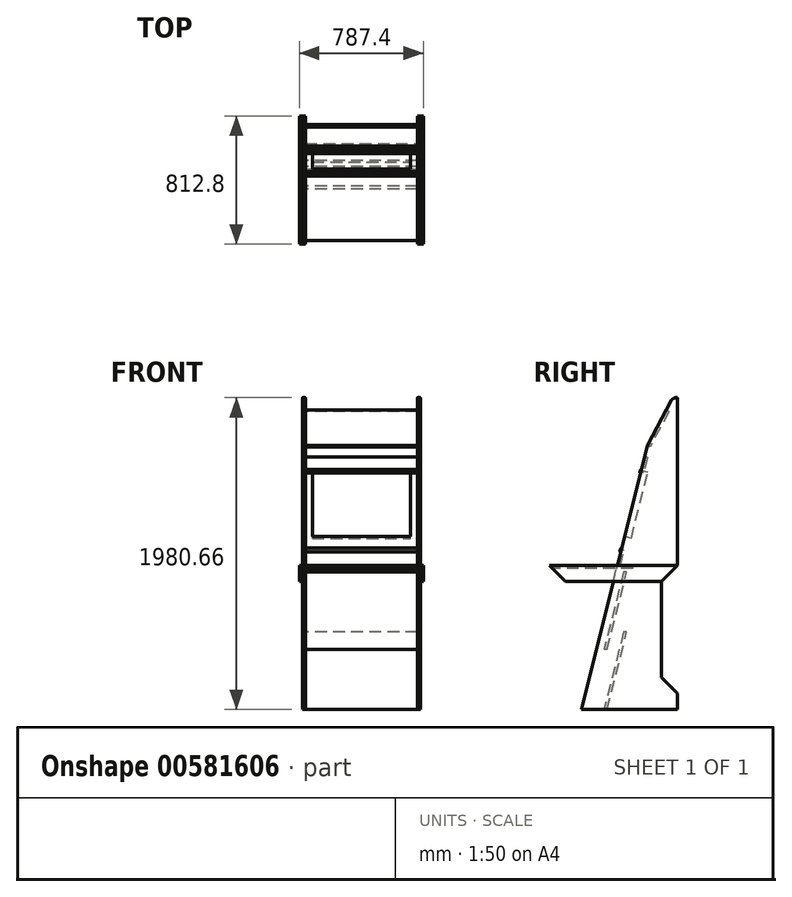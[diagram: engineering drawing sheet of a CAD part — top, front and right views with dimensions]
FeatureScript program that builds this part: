
annotation { "Feature Type Name" : "Feature", "Feature Type Description" : "" }
export const myFeature = defineFeature(function(context is Context, id is Id, definition is map)
    precondition{}
    {
        {
            var Q0;
            Q0=qCreatedBy(makeId("Right.planeOp"),FACE);
            var sketch = newSketch(context, id + "F0", { "sketchPlane" : qUnion([Q0])});
            skLineSegment(sketch, "E0.bottom", {"start": v(0, -978.45) * mm, "end": v(-609.6, -978.45) * mm});
            skLineSegment(sketch, "E0.left", {"start": v(0, -978.45) * mm, "end": v(0, 1053.55) * mm});
            skLineSegment(sketch, "E1", {"start": v(-609.6, -978.45) * mm, "end": v(-190.5, 697.95) * mm});
            skLineSegment(sketch, "E2", {"start": v(0, 1053.55) * mm, "end": v(-190.5, 697.95) * mm});
            skSolve(sketch);
        }
        {
            var Q0;
            Q0 = qSketchRegion(id + "F0", true);
            extrude(context, id + "F1", {"entities" : qUnion([Q0]), "depth" : 19.05 * mm, "offsetDistance" : 25.4 * mm});
        }
        {
            var Q0;
            Q0=makeQuery(id+"F1.opExtrude","CAP_FACE",FACE,{"disambiguationData":[OSD([sQuery(id+"F0.wireOp",EDGE,"E0.bottom"),sQuery(id+"F0.wireOp",EDGE,"E0.left"),sQuery(id+"F0.wireOp",EDGE,"E1"),sQuery(id+"F0.wireOp",EDGE,"E2")])],"isStart":false});
            var sketch = newSketch(context, id + "F2", { "sketchPlane" : qUnion([Q0])});
            skLineSegment(sketch, "E3.bottom", {"start": v(0, -876.85) * mm, "end": v(-101.6, -775.25) * mm});
            skLineSegment(sketch, "E3.left", {"start": v(0, -876.85) * mm, "end": v(0, -64.05) * mm});
            skLineSegment(sketch, "E3.right", {"start": v(-101.6, -775.25) * mm, "end": v(-101.6, -165.65) * mm});
            skLineSegment(sketch, "E4", {"start": v(0, -64.05) * mm, "end": v(-101.6, -165.65) * mm});
            skSolve(sketch);
        }
        {
            var Q0;
            Q0 = qSketchRegion(id + "F2", true);
            extrude(context, id + "F3", {"entities" : qUnion([Q0]), "operationType" : NewBodyOperationType.REMOVE, "oppositeDirection" : true, "depth" : 25.4 * mm, "offsetDistance" : 25.4 * mm});
        }
        {
            var Q0;
            Q0=makeQuery(id+"F1.opExtrude","SWEPT_BODY",BODY,{"disambiguationData":[OSD([sQuery(id+"F0.wireOp",EDGE,"E0.bottom"),sQuery(id+"F0.wireOp",EDGE,"E0.left"),sQuery(id+"F0.wireOp",EDGE,"E1"),sQuery(id+"F0.wireOp",EDGE,"E2")])]});
            transform(context, id + "F4", {"entities" : qUnion([Q0]), "transformType" : TransformType.TRANSLATION_3D, "dx" : 730.25 * mm, "dy" : 0 * mm, "dz" : 0 * mm, "makeCopy" : true});
        }
        {
            var Q0;
            Q0=makeQuery(id+"F4.opPattern","COPY",FACE,{"derivedFrom":makeQuery(id+"F1.opExtrude","CAP_FACE",FACE,{"disambiguationData":[OSD([sQuery(id+"F0.wireOp",EDGE,"E0.bottom"),sQuery(id+"F0.wireOp",EDGE,"E0.left"),sQuery(id+"F0.wireOp",EDGE,"E1"),sQuery(id+"F0.wireOp",EDGE,"E2")])],"isStart":false}),"instanceName":"1"});
            var sketch = newSketch(context, id + "F5", { "sketchPlane" : qUnion([Q0])});
            skLineSegment(sketch, "E5.bottom", {"start": v(0, -64.05) * mm, "end": v(-812.8, -64.05) * mm});
            skLineSegment(sketch, "E5.left", {"start": v(0, -64.05) * mm, "end": v(-101.6, -165.65) * mm});
            skLineSegment(sketch, "E6", {"start": v(-101.6, -165.65) * mm, "end": v(-711.2, -165.65) * mm});
            skLineSegment(sketch, "E7", {"start": v(-711.2, -165.65) * mm, "end": v(-812.8, -64.05) * mm});
            skSolve(sketch);
        }
        {
            var Q0;
            {var subQ0=sQuery(id+"F5.wireOp",EDGE,"E5.left");Q0=makeQuery(id+"F5.imprint","IMPRINT",FACE,{"disambiguationData":[TD([[makeQuery(id+"F5.imprint","IMPRINT",EDGE,{"derivedFrom":subQ0}),-1.0]])]});}
            var Q1;
            {var subQ0=sQuery(id+"F5.wireOp",EDGE,"E7");Q1=makeQuery(id+"F5.imprint","IMPRINT",FACE,{"disambiguationData":[TD([[makeQuery(id+"F5.imprint","IMPRINT",EDGE,{"derivedFrom":subQ0}),-1.0]])]});}
            extrude(context, id + "F6", {"entities" : qUnion([Q0, Q1]), "depth" : 19.05 * mm, "offsetDistance" : 25.4 * mm});
        }
        {
            var Q0;
            Q0=makeQuery(id+"F6.opExtrude","SWEPT_BODY",BODY,{"disambiguationData":[OSD([sQuery(id+"F5.wireOp",EDGE,"E5.bottom"),sQuery(id+"F5.wireOp",EDGE,"E5.left"),sQuery(id+"F5.wireOp",EDGE,"E6"),sQuery(id+"F5.wireOp",EDGE,"E7")])]});
            transform(context, id + "F7", {"entities" : qUnion([Q0]), "transformType" : TransformType.TRANSLATION_3D, "dx" : -768.35 * mm, "dy" : 0 * mm, "dz" : 0 * mm, "makeCopy" : true});
        }
        {
            var Q0;
            Q0=makeQuery(id+"F1.opExtrude","CAP_FACE",FACE,{"disambiguationData":[OSD([sQuery(id+"F0.wireOp",EDGE,"E0.bottom"),sQuery(id+"F0.wireOp",EDGE,"E0.left"),sQuery(id+"F0.wireOp",EDGE,"E1"),sQuery(id+"F0.wireOp",EDGE,"E2")])],"isStart":false});
            var sketch = newSketch(context, id + "F8", { "sketchPlane" : qUnion([Q0])});
            skLineSegment(sketch, "E8", {"start": v(-464.22, -978.45) * mm, "end": v(-445.17, -978.45) * mm});
            skLineSegment(sketch, "E9", {"start": v(-445.17, -978.45) * mm, "end": v(-321.96, -485.62) * mm});
            skLineSegment(sketch, "E10", {"start": v(-321.96, -485.62) * mm, "end": v(-341.01, -485.62) * mm});
            skLineSegment(sketch, "E11", {"start": v(-341.01, -485.62) * mm, "end": v(-464.22, -978.45) * mm});
            skSolve(sketch);
        }
        {
            var Q0;
            Q0 = qSketchRegion(id + "F8", true);
            extrude(context, id + "F9", {"entities" : qUnion([Q0]), "depth" : 711.2 * mm, "offsetDistance" : 25.4 * mm});
        }
        {
            var Q0;
            Q0=makeQuery(id+"F9.opExtrude","SWEPT_BODY",BODY,{"disambiguationData":[OSD([sQuery(id+"F8.wireOp",EDGE,"E8"),sQuery(id+"F8.wireOp",EDGE,"E9"),sQuery(id+"F8.wireOp",EDGE,"E10"),sQuery(id+"F8.wireOp",EDGE,"E11")])]});
            transform(context, id + "F10", {"entities" : qUnion([Q0]), "transformType" : TransformType.TRANSLATION_3D, "dx" : 0 * mm, "dy" : 0 * mm, "dz" : 381 * mm, "makeCopy" : true});
        }
        {
            var Q0;
            Q0=makeQuery(id+"F7.opPattern","COPY",FACE,{"derivedFrom":makeQuery(id+"F6.opExtrude","SWEPT_FACE",FACE,{"disambiguationData":[OSD([sQuery(id+"F5.wireOp",EDGE,"E5.bottom")])]}),"instanceName":"1"});
            var sketch = newSketch(context, id + "F11", { "sketchPlane" : qUnion([Q0])});
            skLineSegment(sketch, "E12", {"start": v(19.05, -281.53) * mm, "end": v(19.05, -789.53) * mm});
            skLineSegment(sketch, "E13", {"start": v(19.05, -789.53) * mm, "end": v(730.25, -789.53) * mm});
            skLineSegment(sketch, "E14", {"start": v(730.25, -789.53) * mm, "end": v(730.25, -281.53) * mm});
            skLineSegment(sketch, "E15", {"start": v(730.25, -281.53) * mm, "end": v(19.05, -281.53) * mm});
            skSolve(sketch);
        }
        {
            var Q0;
            Q0 = qSketchRegion(id + "F11", true);
            extrude(context, id + "F12", {"entities" : qUnion([Q0]), "oppositeDirection" : true, "depth" : 19.05 * mm, "offsetDistance" : 25.4 * mm});
        }
        {
            var Q0;
            {var subQ0=sQuery(id+"F5.wireOp",EDGE,"E7");Q0=makeQuery(id+"F5.imprint","IMPRINT",FACE,{"disambiguationData":[TD([[makeQuery(id+"F5.imprint","IMPRINT",EDGE,{"derivedFrom":subQ0}),-1.0]])]});}
            extrude(context, id + "F13", {"entities" : qUnion([Q0]), "oppositeDirection" : true, "depth" : 19.05 * mm, "offsetDistance" : 25.4 * mm});
        }
        {
            var Q0;
            Q0=makeQuery(id+"F13.opExtrude","SWEPT_BODY",BODY,{"disambiguationData":[OSD([sQuery(id+"F0.wireOp",EDGE,"E1"),sQuery(id+"F5.wireOp",EDGE,"E5.bottom"),sQuery(id+"F5.wireOp",EDGE,"E6"),sQuery(id+"F5.wireOp",EDGE,"E7")])]});
            transform(context, id + "F14", {"entities" : qUnion([Q0]), "transformType" : TransformType.TRANSLATION_3D, "dx" : -730.25 * mm, "dy" : 0 * mm, "dz" : 0 * mm, "makeCopy" : true});
        }
        {
            var Q0;
            Q0=makeQuery(id+"F1.opExtrude","SWEPT_FACE",FACE,{"disambiguationData":[OSD([sQuery(id+"F0.wireOp",EDGE,"E1")])]});
            var sketch = newSketch(context, id + "F15", { "sketchPlane" : qUnion([Q0])});
            skLineSegment(sketch, "E16", {"start": v(63.5, 466.48) * mm, "end": v(63.5, 34.68) * mm});
            skLineSegment(sketch, "E17", {"start": v(63.5, 34.68) * mm, "end": v(685.8, 34.68) * mm});
            skLineSegment(sketch, "E18", {"start": v(685.8, 34.68) * mm, "end": v(685.8, 466.48) * mm});
            skLineSegment(sketch, "E19", {"start": v(685.8, 466.48) * mm, "end": v(63.5, 466.48) * mm});
            skLineSegment(sketch, "E20", {"start": v(374.65, 466.48) * mm, "end": v(374.65, 34.68) * mm});
            skSolve(sketch);
        }
        {
            var Q0;
            Q0 = qSketchRegion(id + "F15", true);
            extrude(context, id + "F16", {"entities" : qUnion([Q0]), "oppositeDirection" : true, "depth" : 44.45 * mm, "offsetDistance" : 25.4 * mm});
        }
        {
            var Q0;
            Q0=makeQuery(id+"F1.opExtrude","SWEPT_FACE",FACE,{"disambiguationData":[OSD([sQuery(id+"F0.wireOp",EDGE,"E1")])]});
            var sketch = newSketch(context, id + "F17", { "sketchPlane" : qUnion([Q0])});
            skLineSegment(sketch, "E21", {"start": v(19.05, -52.36) * mm, "end": v(730.25, -52.36) * mm});
            skLineSegment(sketch, "E22", {"start": v(19.05, -153.96) * mm, "end": v(730.82, -153.96) * mm});
            skLineSegment(sketch, "E23", {"start": v(19.05, -52.36) * mm, "end": v(19.05, -153.96) * mm});
            skLineSegment(sketch, "E24", {"start": v(730.25, -52.36) * mm, "end": v(730.82, -153.96) * mm});
            skSolve(sketch);
        }
        {
            var Q0;
            Q0 = qSketchRegion(id + "F17", true);
            extrude(context, id + "F18", {"entities" : qUnion([Q0]), "oppositeDirection" : true, "depth" : 19.05 * mm, "offsetDistance" : 25.4 * mm});
        }
        {
            var Q0;
            Q0=makeQuery(id+"F18.opExtrude","CAP_FACE",FACE,{"disambiguationData":[OSD([sQuery(id+"F17.wireOp",EDGE,"E21"),sQuery(id+"F17.wireOp",EDGE,"E22"),sQuery(id+"F17.wireOp",EDGE,"E23"),sQuery(id+"F17.wireOp",EDGE,"E24")])],"isStart":true});
            var sketch = newSketch(context, id + "F19", { "sketchPlane" : qUnion([Q0])});
            skLineSegment(sketch, "E25", {"start": v(19.05, 455.64) * mm, "end": v(730.25, 455.64) * mm});
            skLineSegment(sketch, "E26", {"start": v(730.25, 455.64) * mm, "end": v(730.25, 557.24) * mm});
            skLineSegment(sketch, "E27", {"start": v(730.25, 557.24) * mm, "end": v(19.05, 557.24) * mm});
            skLineSegment(sketch, "E28", {"start": v(19.05, 557.24) * mm, "end": v(19.05, 455.64) * mm});
            skSolve(sketch);
        }
        {
            var Q0;
            Q0 = qSketchRegion(id + "F19", true);
            extrude(context, id + "F20", {"entities" : qUnion([Q0]), "oppositeDirection" : true, "depth" : 19.05 * mm, "offsetDistance" : 25.4 * mm});
        }
        {
            var Q0;
            Q0=makeQuery(id+"F16.opExtrude","CAP_FACE",FACE,{"disambiguationData":[OSD([sQuery(id+"F15.wireOp",EDGE,"E16"),sQuery(id+"F15.wireOp",EDGE,"E17"),sQuery(id+"F15.wireOp",EDGE,"E18"),sQuery(id+"F15.wireOp",EDGE,"E19")])],"isStart":true});
            var sketch = newSketch(context, id + "F21", { "sketchPlane" : qUnion([Q0])});
            skLineSegment(sketch, "E29", {"start": v(19.05, 455.64) * mm, "end": v(730.25, 455.64) * mm});
            skLineSegment(sketch, "E30", {"start": v(730.25, 455.64) * mm, "end": v(730.25, -52.36) * mm});
            skLineSegment(sketch, "E31", {"start": v(730.25, -52.36) * mm, "end": v(19.05, -52.36) * mm});
            skLineSegment(sketch, "E32", {"start": v(19.05, -52.36) * mm, "end": v(19.05, 455.64) * mm});
            skSolve(sketch);
        }
        {
            var Q0;
            Q0 = qSketchRegion(id + "F21", true);
            extrude(context, id + "F22", {"entities" : qUnion([Q0]), "oppositeDirection" : true, "depth" : 5.08 * mm, "offsetDistance" : 25.4 * mm});
        }
        {
            var Q0;
            Q0=makeQuery(id+"F1.opExtrude","SWEPT_FACE",FACE,{"disambiguationData":[OSD([sQuery(id+"F0.wireOp",EDGE,"E2")])]});
            var sketch = newSketch(context, id + "F23", { "sketchPlane" : qUnion([Q0])});
            skLineSegment(sketch, "E33", {"start": v(19.05, 525.27) * mm, "end": v(730.25, 525.27) * mm});
            skLineSegment(sketch, "E34", {"start": v(730.25, 525.27) * mm, "end": v(730.25, 779.27) * mm});
            skLineSegment(sketch, "E35", {"start": v(730.25, 779.27) * mm, "end": v(19.05, 779.27) * mm});
            skLineSegment(sketch, "E36", {"start": v(19.05, 779.27) * mm, "end": v(19.05, 525.27) * mm});
            skSolve(sketch);
        }
        {
            var Q0;
            Q0 = qSketchRegion(id + "F23", true);
            extrude(context, id + "F24", {"entities" : qUnion([Q0]), "oppositeDirection" : true, "depth" : 19.05 * mm, "offsetDistance" : 25.4 * mm});
        }
        {
            var Q0;
            Q0=makeQuery(id+"F18.opExtrude","CAP_FACE",FACE,{"disambiguationData":[OSD([sQuery(id+"F17.wireOp",EDGE,"E21"),sQuery(id+"F17.wireOp",EDGE,"E22"),sQuery(id+"F17.wireOp",EDGE,"E23"),sQuery(id+"F17.wireOp",EDGE,"E24")])],"isStart":true});
            var sketch = newSketch(context, id + "F25", { "sketchPlane" : qUnion([Q0])});
            skLineSegment(sketch, "E37", {"start": v(19.12, -39.66) * mm, "end": v(19.12, -65.06) * mm});
            skLineSegment(sketch, "E38", {"start": v(19.12, -65.06) * mm, "end": v(730.32, -65.06) * mm});
            skLineSegment(sketch, "E39", {"start": v(730.32, -65.06) * mm, "end": v(730.32, -39.66) * mm});
            skLineSegment(sketch, "E40", {"start": v(730.32, -39.66) * mm, "end": v(19.12, -39.66) * mm});
            skLineSegment(sketch, "E41", {"start": v(19.12, -52.36) * mm, "end": v(730.32, -52.36) * mm});
            skSolve(sketch);
        }
        {
            var Q0;
            Q0 = qSketchRegion(id + "F25", true);
            extrude(context, id + "F26", {"entities" : qUnion([Q0]), "depth" : 5.08 * mm, "offsetDistance" : 25.4 * mm});
        }
        {
            var Q0;
            Q0=makeQuery(id+"F26.opExtrude","CAP_EDGE",EDGE,{"disambiguationData":[OSD([sQuery(id+"F25.wireOp",EDGE,"E40")])],"isStart":false});
            var Q1;
            Q1=makeQuery(id+"F26.opExtrude","CAP_EDGE",EDGE,{"disambiguationData":[OSD([sQuery(id+"F25.wireOp",EDGE,"E38")])],"isStart":false});
            fillet(context, id + "F27", {"entities" : qUnion([Q0, Q1]), "radius" : 5.08 * mm, "tangentPropagation" : true, "allowEdgeOverflow" : false});
        }
        {
            var Q0;
            Q0=makeQuery(id+"F26.opExtrude","SWEPT_BODY",BODY,{"disambiguationData":[OSD([sQuery(id+"F25.wireOp",EDGE,"E37"),sQuery(id+"F25.wireOp",EDGE,"E38"),sQuery(id+"F25.wireOp",EDGE,"E39"),sQuery(id+"F25.wireOp",EDGE,"E40")])]});
            transform(context, id + "F28", {"entities" : qUnion([Q0]), "transformType" : TransformType.TRANSLATION_3D, "dx" : 0 * mm, "dy" : 124.7 * mm, "dz" : 499.36 * mm, "makeCopy" : true});
        }
        {
            var Q0;
            Q0=makeQuery(id+"F4.opPattern","COPY",FACE,{"derivedFrom":makeQuery(id+"F1.opExtrude","CAP_FACE",FACE,{"disambiguationData":[OSD([sQuery(id+"F0.wireOp",EDGE,"E0.bottom"),sQuery(id+"F0.wireOp",EDGE,"E0.left"),sQuery(id+"F0.wireOp",EDGE,"E1"),sQuery(id+"F0.wireOp",EDGE,"E2")])],"isStart":false}),"instanceName":"1"});
            var sketch = newSketch(context, id + "F29", { "sketchPlane" : qUnion([Q0])});
            skPoint(sketch, "E42", {"position": v(-35.98, 986.38) * mm});
            skArc(sketch, "E43", {"start": v(-35.98, 986.38) * mm, "mid": v(-19.65, 998.08) * mm, "end": v(0, 1002.2) * mm});
            skLineSegment(sketch, "E44", {"start": v(0, 1002.2) * mm, "end": v(0, 1053.55) * mm});
            skLineSegment(sketch, "E45", {"start": v(0, 1053.55) * mm, "end": v(-35.98, 986.38) * mm});
            skSolve(sketch);
        }
        {
            var Q0;
            Q0 = qSketchRegion(id + "F29", true);
            extrude(context, id + "F30", {"entities" : qUnion([Q0]), "operationType" : NewBodyOperationType.REMOVE, "oppositeDirection" : true, "depth" : 762 * mm, "offsetDistance" : 25.4 * mm});
        }
    });
